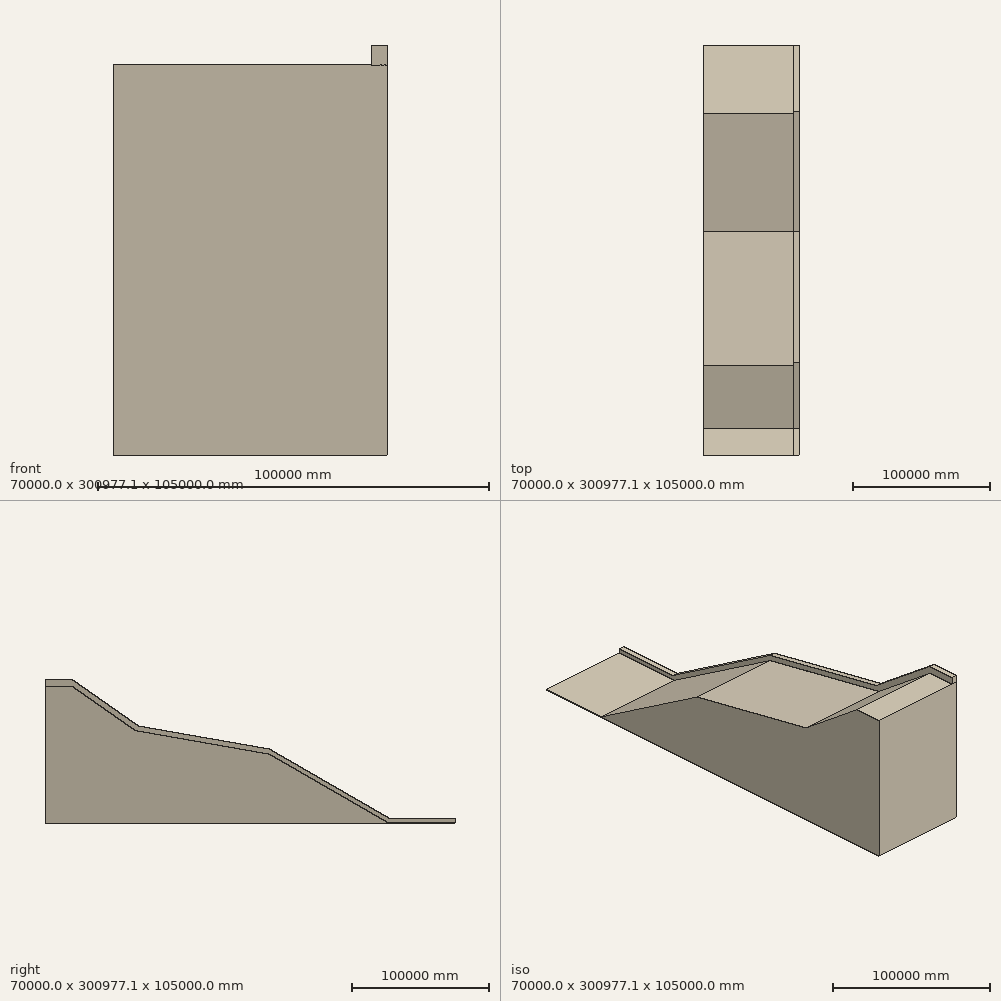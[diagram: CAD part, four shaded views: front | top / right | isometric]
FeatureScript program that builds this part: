
annotation { "Feature Type Name" : "Feature", "Feature Type Description" : "" }
export const myFeature = defineFeature(function(context is Context, id is Id, definition is map)
    precondition{}
    {
        {
            var Q0;
            Q0=qCreatedBy(makeId("Top.planeOp"),FACE);
            var sketch = newSketch(context, id + "F0", { "sketchPlane" : qUnion([Q0])});
            skLineSegment(sketch, "E0.bottom", {"start": v(35000, 25000) * mm, "end": v(-35000, 25000) * mm});
            skLineSegment(sketch, "E0.top", {"start": v(35000, -25000) * mm, "end": v(-35000, -25000) * mm});
            skLineSegment(sketch, "E0.left", {"start": v(35000, 25000) * mm, "end": v(35000, -25000) * mm});
            skLineSegment(sketch, "E0.right", {"start": v(-35000, 25000) * mm, "end": v(-35000, -25000) * mm});
            skSolve(sketch);
        }
        {
            var Q0;
            Q0 = qSketchRegion(id + "F0", true);
            extrude(context, id + "F1", {"entities" : qUnion([Q0]), "endBound" : BoundingType.SYMMETRIC, "depth" : 500 * mm, "offsetDistance" : 25 * mm});
        }
        {
            var Q0;
            Q0=qCreatedBy(makeId("Right.planeOp"),FACE);
            var sketch = newSketch(context, id + "F2", { "sketchPlane" : qUnion([Q0])});
            skPoint(sketch, "E1.0", {"position": v(-25000, 250) * mm});
            skLineSegment(sketch, "E2", {"start": v(-25000, 250) * mm, "end": v(-111602.54, 50250) * mm});
            skLineSegment(sketch, "E3", {"start": v(-111602.54, 50250) * mm, "end": v(-210083.32, 67614.82) * mm});
            skLineSegment(sketch, "E4", {"start": v(-210083.32, 67614.82) * mm, "end": v(-255977.11, 99750) * mm});
            skLineSegment(sketch, "E5", {"start": v(-255977.11, 99750) * mm, "end": v(-275977.11, 99750) * mm});
            skLineSegment(sketch, "E6", {"start": v(-275977.11, 99750) * mm, "end": v(-275977.11, -250) * mm});
            skPoint(sketch, "E7.0", {"position": v(-25000, -250) * mm});
            skLineSegment(sketch, "E8", {"start": v(-25000, -250) * mm, "end": v(-275977.11, -250) * mm});
            skPoint(sketch, "E9.0", {"position": v(-25000, 0) * mm});
            skLineSegment(sketch, "E10.0", {"start": v(-25000, 250) * mm, "end": v(-25000, -250) * mm});
            skSolve(sketch);
        }
        {
            var Q0;
            Q0=makeQuery(id+"F2.imprint","IMPRINT",FACE,{"disambiguationData":[TD([[makeQuery(id+"F2.imprint","IMPRINT",EDGE,{"derivedFrom":sQuery(id+"F2.wireOp",EDGE,"E2")}),1.0]])]});
            extrude(context, id + "F3", {"entities" : qUnion([Q0]), "operationType" : NewBodyOperationType.ADD, "endBound" : BoundingType.SYMMETRIC, "depth" : 70000 * mm, "offsetDistance" : 25 * mm});
        }
        {
            var Q0;
            Q0=makeQuery(id+"F3.boolean.opBoolean","MERGE",FACE,{"derivedFrom":[makeQuery(id+"F1.opExtrude","SWEPT_FACE",FACE,{"disambiguationData":[OSD([sQuery(id+"F0.wireOp",EDGE,"E0.left")])]}),makeQuery(id+"F3.opExtrude","CAP_FACE",FACE,{"disambiguationData":[OSD([sQuery(id+"F2.wireOp",EDGE,"E2"),sQuery(id+"F2.wireOp",EDGE,"E3"),sQuery(id+"F2.wireOp",EDGE,"E4"),sQuery(id+"F2.wireOp",EDGE,"E5"),sQuery(id+"F2.wireOp",EDGE,"E6"),sQuery(id+"F2.wireOp",EDGE,"E8"),sQuery(id+"F2.wireOp",EDGE,"E10.0")])],"isStart":false})]});
            var sketch = newSketch(context, id + "F4", { "sketchPlane" : qUnion([Q0])});
            skPoint(sketch, "E11.0", {"position": v(-265977.11, 99750) * mm});
            skLineSegment(sketch, "E12.0", {"start": v(-255977.11, 99750) * mm, "end": v(-275977.11, 99750) * mm});
            skLineSegment(sketch, "E13.0.0", {"start": v(-210083.32, 67614.82) * mm, "end": v(-255977.11, 99750) * mm});
            skLineSegment(sketch, "E13.0.2", {"start": v(-255977.11, 99750) * mm, "end": v(-210083.32, 67614.82) * mm});
            skLineSegment(sketch, "E14.0", {"start": v(-111602.54, 50250) * mm, "end": v(-210083.32, 67614.82) * mm});
            skLineSegment(sketch, "E15.0", {"start": v(-25000, 250) * mm, "end": v(-111602.54, 50250) * mm});
            skLineSegment(sketch, "E16.0", {"start": v(25000, 250) * mm, "end": v(-25000, 250) * mm});
            skLineSegment(sketch, "E17", {"start": v(-275977.11, 99750) * mm, "end": v(-275977.11, 104750) * mm});
            skLineSegment(sketch, "E18", {"start": v(-275977.11, 104750) * mm, "end": v(-255977.11, 104750) * mm});
            skLineSegment(sketch, "E19", {"start": v(-255977.11, 104750) * mm, "end": v(-248836.37, 99750) * mm});
            skLineSegment(sketch, "E20", {"start": v(-248836.37, 99750) * mm, "end": v(-207768.83, 70994.2) * mm});
            skLineSegment(sketch, "E21", {"start": v(-207768.83, 70994.2) * mm, "end": v(-111602.54, 54037.48) * mm});
            skLineSegment(sketch, "E22", {"start": v(-111602.54, 54037.48) * mm, "end": v(-23375.58, 3099.62) * mm});
            skLineSegment(sketch, "E23", {"start": v(-23375.58, 3099.62) * mm, "end": v(25000, 3099.62) * mm});
            skLineSegment(sketch, "E24", {"start": v(25000, 3099.62) * mm, "end": v(25000, 250) * mm});
            skSolve(sketch);
        }
        {
            var Q0;
            Q0=makeQuery(id+"F4.imprint","IMPRINT",FACE,{"disambiguationData":[TD([[makeQuery(id+"F4.imprint","IMPRINT",EDGE,{"derivedFrom":sQuery(id+"F4.wireOp",EDGE,"E12.0")}),-1.0]])]});
            extrude(context, id + "F5", {"entities" : qUnion([Q0]), "oppositeDirection" : true, "depth" : 4000 * mm, "offsetDistance" : 25 * mm});
        }
    });
